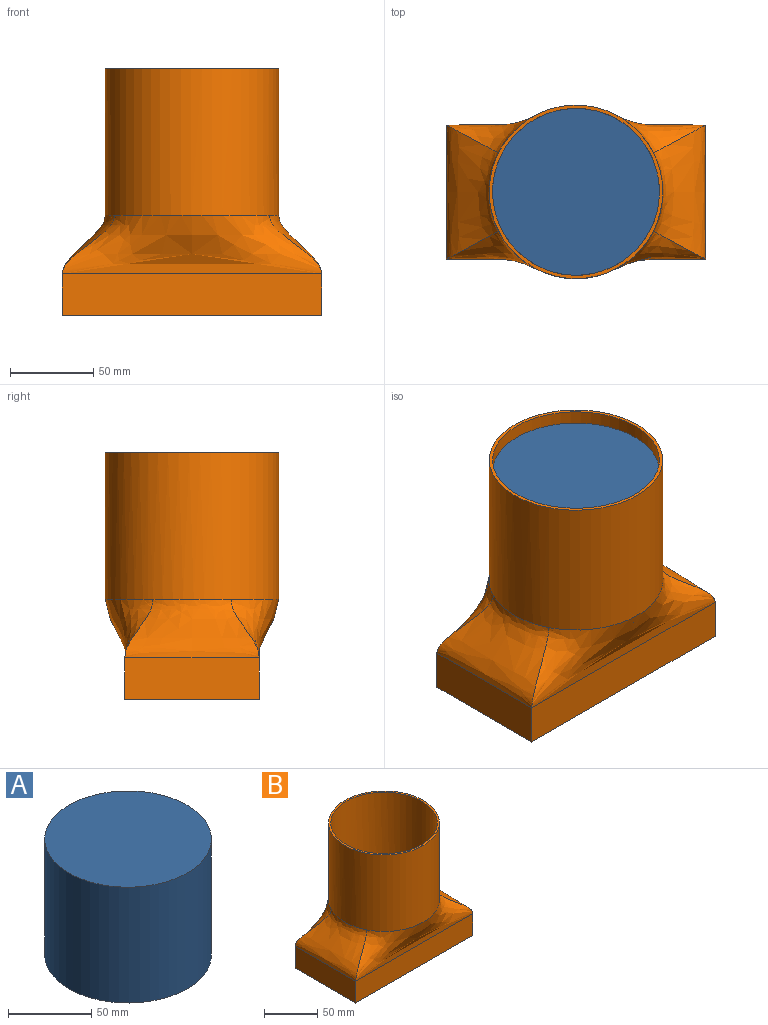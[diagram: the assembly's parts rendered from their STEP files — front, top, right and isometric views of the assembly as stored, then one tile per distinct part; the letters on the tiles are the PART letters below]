
ASSEMBLY  parts=2 mates=1
PART A: 3 faces, bbox 100x100x85 mm
  f0: cylinder r=50mm len=100mm, axis (0,0,-1), area 26703.5mm2, adj f1,f2
  f1: plane 100x100mm, normal (0,0,1), area 7854mm2, adj f0
  f2: plane 100x100mm, normal (0,0,-1), area 7854mm2, adj f0
PART B: 20 faces, bbox 155.3x104x148 mm
  f0: plane 151.3x25mm, normal (0,-1,0), area 3782.5mm2, adj f1,f7,f8,f15
  f1: plane 76.4x25mm, normal (-1,0,0), area 1910mm2, adj f0,f2,f8,f13
  f2: plane 151.3x25mm, normal (0,1,0), area 3782.5mm2, adj f1,f7,f8,f18
  f3: plane 80.4x25mm, normal (1,0,0), area 2010mm2, adj f4,f6,f8,f12
  f4: plane 155.3x25mm, normal (0,1,0), area 3882.5mm2, adj f3,f5,f8,f14
  f5: plane 80.4x25mm, normal (-1,0,0), area 2010mm2, adj f4,f6,f8,f17
  f6: plane 155.3x25mm, normal (0,-1,0), area 3882.5mm2, adj f3,f5,f8,f19
  f7: plane 76.4x25mm, normal (1,0,0), area 1910mm2, adj f0,f2,f8,f16
  f8: plane 155.3x80.4mm, normal (0,0,-1), area 926.8mm2, adj f0,f1,f2,f3,f4,f5,f6,f7
  f9: cylinder r=52mm len=104mm, axis (0,0,-1), area 28751.9mm2, adj f11,f12,f14,f17,f19
  f10: cylinder r=50mm len=100mm, axis (0,0,-1), area 27646mm2, adj f11,f13,f15,f16,f18
  f11: plane 104x104mm, normal (0,0,1), area 640.9mm2, adj f9,f10
  f12: bspline ~80.4x35mm, area 2973.9mm2, adj f3,f9,f14,f19
  f13: bspline ~76.4x35mm, area 2832.9mm2, adj f1,f10,f15,f18
  f14: bspline ~155.3x35mm, area 4909.4mm2, adj f4,f9,f12,f17
  f15: bspline ~151.3x35mm, area 4741.9mm2, adj f0,f10,f13,f16
  f16: bspline ~76.4x35mm, area 2832.9mm2, adj f7,f10,f15,f18
  f17: bspline ~80.4x35mm, area 2973.9mm2, adj f5,f9,f14,f19
  f18: bspline ~151.3x35mm, area 4741.9mm2, adj f2,f10,f13,f16
  f19: bspline ~155.3x35mm, area 4909.4mm2, adj f6,f9,f12,f17
PLACE A t=(4.75,-32.54,-93.24)mm
PLACE B t=(-238.36,41.5,-88)mm fixed
MATE slider B.f10 <-> A.f0  axis (0,0,1) through (-238.36,41.5,35)mm
